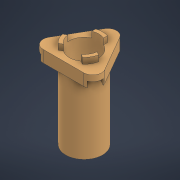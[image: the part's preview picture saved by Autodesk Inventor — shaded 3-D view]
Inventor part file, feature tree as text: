
AUTODESK INVENTOR PART (.ipt)
format: ipt  version: 2021 (Build 250183000, 183)  size: 223,744 bytes
history: native  units: mm
features: other x6, extrude x4, sketch x4
ambient origin geometry x8: Origin, YZ Plane, XZ Plane, XY Plane, X Axis, Y Axis, Z Axis, Center Point
bodies: Body1 (feature_tree), Body2 (feature_tree)
feature tree (14):
  other  "Suporte Contato"
  other  "Sólido1"
  extrude  "Extrusão1"  Depth=1.0mm
  extrude  "Extrusão2"  Depth=2.8mm
  extrude  "Extrusão3"  Depth=30.0mm TaperAngle=360.0deg
  extrude  "Extrusão4"  Depth=0.4mm TaperAngle=0.0deg
  sketch  "Esboço1"  dims[d0=1.25mm d1=1.0mm]
  sketch  "Esboço2"  dims[d2=2.8mm d3=0.0mm d5=1.4mm]
  other  "Contorno projetado1"
  sketch  "Esboço3"  dims[d6=1.4mm d7=30.0mm d9=360.0deg]
  other  "Contorno projetado2"
  other  "Contorno projetado3"
  sketch  "Esboço4"  dims[d11=0.3mm d12=0.4mm d13=0.0mm d14=0.4mm d15=30.0mm d17=360.0deg d20=1.35mm d21=0.2mm d22=0.0mm d23=1.2mm d24=1.0mm d25=0.2mm d26=0.0mm]
  other  "Contorno projetado4"
